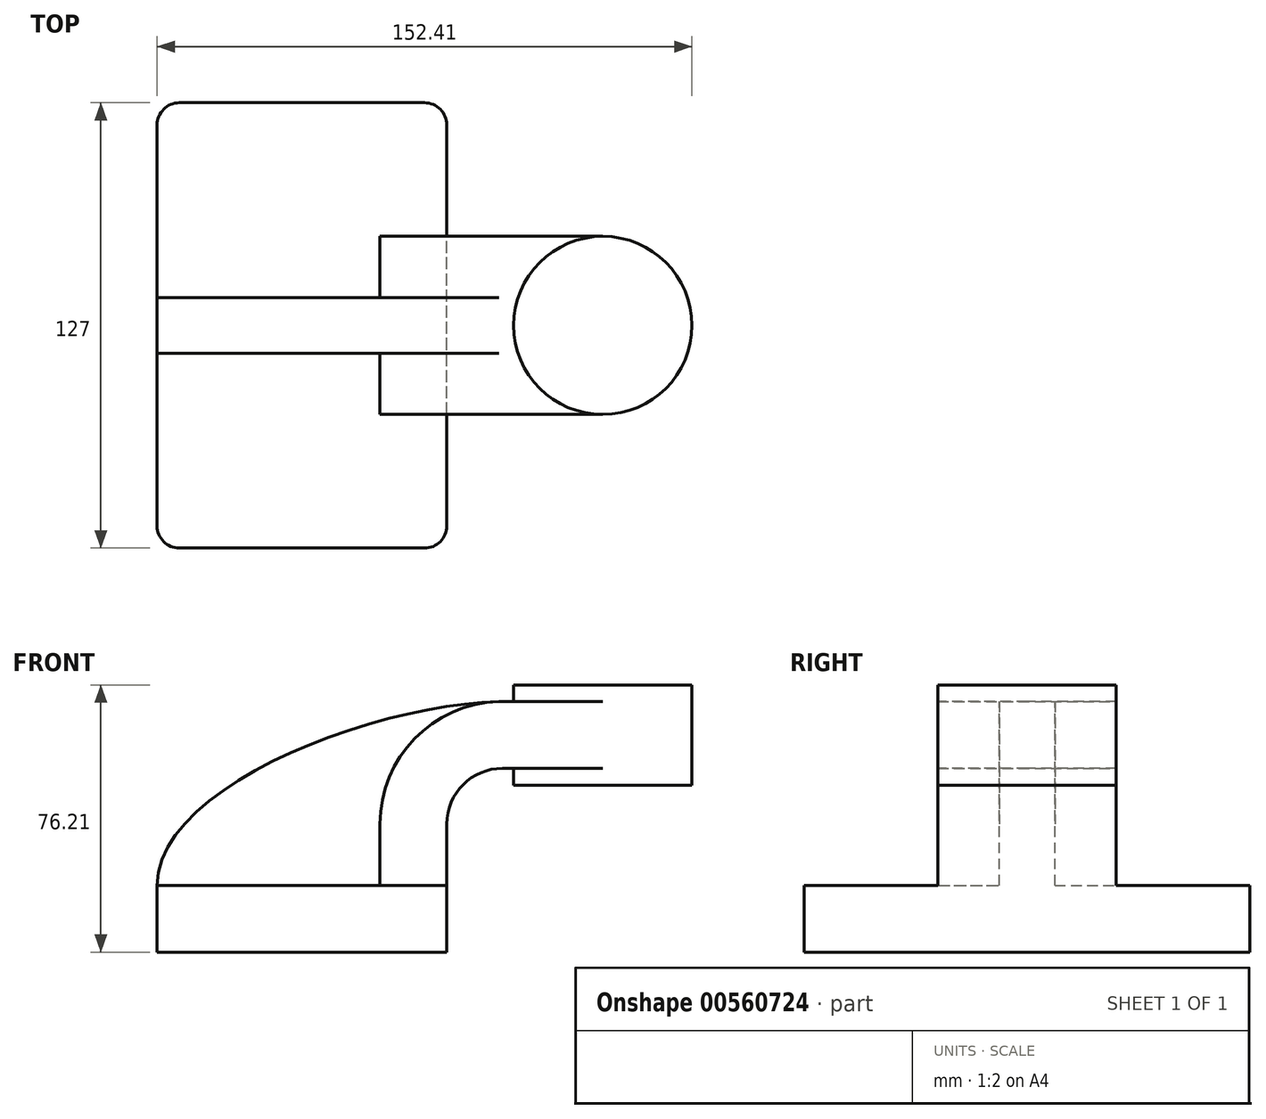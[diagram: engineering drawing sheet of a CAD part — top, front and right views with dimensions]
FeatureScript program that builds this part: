
annotation { "Feature Type Name" : "Feature", "Feature Type Description" : "" }
export const myFeature = defineFeature(function(context is Context, id is Id, definition is map)
    precondition{}
    {
        {
            var Q0;
            Q0=qCreatedBy(makeId("Front.planeOp"),FACE);
            var sketch = newSketch(context, id + "F0", { "sketchPlane" : qUnion([Q0])});
            skLineSegment(sketch, "E0.bottom", {"start": v(41.28, -9.52) * mm, "end": v(-41.28, -9.53) * mm});
            skLineSegment(sketch, "E0.top", {"start": v(41.27, 9.53) * mm, "end": v(-41.28, 9.53) * mm});
            skLineSegment(sketch, "E0.left", {"start": v(41.28, -9.52) * mm, "end": v(41.28, 9.53) * mm});
            skLineSegment(sketch, "E0.right", {"start": v(-41.28, -9.52) * mm, "end": v(-41.28, 9.53) * mm});
            skPoint(sketch, "E0.middle", {"position": v(0, 0) * mm});
            skLineSegment(sketch, "E1.bottom", {"start": v(60.32, 38.1) * mm, "end": v(111.12, 38.1) * mm});
            skLineSegment(sketch, "E1.top", {"start": v(60.32, 66.68) * mm, "end": v(111.12, 66.68) * mm});
            skLineSegment(sketch, "E1.left", {"start": v(60.32, 38.1) * mm, "end": v(60.32, 66.68) * mm});
            skLineSegment(sketch, "E1.right", {"start": v(111.12, 38.1) * mm, "end": v(111.12, 66.68) * mm});
            skPoint(sketch, "E1.middle", {"position": v(85.72, 52.39) * mm});
            skLineSegment(sketch, "E2", {"start": v(41.27, 9.53) * mm, "end": v(41.27, 27) * mm});
            skArc(sketch, "E3", {"start": v(41.27, 27) * mm, "mid": v(45.92, 38.23) * mm, "end": v(57.15, 42.88) * mm});
            skLineSegment(sketch, "E4", {"start": v(57.15, 42.88) * mm, "end": v(85.72, 42.88) * mm});
            skLineSegment(sketch, "E5.0", {"start": v(57.15, 61.93) * mm, "end": v(85.72, 61.93) * mm});
            skArc(sketch, "E5.1", {"start": v(22.23, 27) * mm, "mid": v(32.45, 51.7) * mm, "end": v(57.15, 61.93) * mm});
            skLineSegment(sketch, "E5.2", {"start": v(22.23, 9.53) * mm, "end": v(22.23, 27) * mm});
            skFitSpline(sketch, "E6", {"points": [v(-41.28, 9.53) * mm, v(57.15, 61.93) * mm], "startDerivative": vector(0.33, 86.27) * mm, "endDerivative": vector(105.39, 0.93) * mm});
            skLineSegment(sketch, "E7", {"start": v(85.72, 38.1) * mm, "end": v(85.72, 66.68) * mm});
            skSolve(sketch);
        }
        {
            var Q0;
            Q0=makeQuery(id+"F0.imprint","IMPRINT",FACE,{"disambiguationData":[TD([[makeQuery(id+"F0.imprint","IMPRINT",EDGE,{"derivedFrom":sQuery(id+"F0.wireOp",EDGE,"E0.bottom")}),-1.0]])]});
            extrude(context, id + "F1", {"entities" : qUnion([Q0]), "endBound" : BoundingType.SYMMETRIC, "depth" : 127 * mm, "offsetDistance" : 25.4 * mm});
        }
        {
            var Q0;
            {var subQ0=sQuery(id+"F0.wireOp",EDGE,"E4");var subQ1=sQuery(id+"F0.wireOp",EDGE,"E1.left");var subQ2=makeQuery(id+"F0.imprint","INTERSECT",VERTEX,{"derivedFrom":[subQ1,subQ0]});Q0=makeQuery(id+"F0.imprint","IMPRINT",FACE,{"disambiguationData":[TD([[makeQuery(id+"F0.imprint","IMPRINT",EDGE,{"disambiguationData":[TD([[subQ2,-1.0]])],"derivedFrom":subQ1}),-1.0]])]});}
            var Q1;
            {var subQ1=sQuery(id+"F0.wireOp",EDGE,"E2");Q1=makeQuery(id+"F0.imprint","IMPRINT",FACE,{"disambiguationData":[TD([[makeQuery(id+"F0.imprint","IMPRINT",EDGE,{"derivedFrom":subQ1}),1.0]])]});}
            extrude(context, id + "F2", {"entities" : qUnion([Q0, Q1]), "operationType" : NewBodyOperationType.ADD, "endBound" : BoundingType.SYMMETRIC, "depth" : 50.8 * mm, "offsetDistance" : 25.4 * mm});
        }
        {
            var Q0;
            {var subQ3=sQuery(id+"F0.wireOp",EDGE,"E5.2");Q0=makeQuery(id+"F0.imprint","IMPRINT",FACE,{"disambiguationData":[TD([[makeQuery(id+"F0.imprint","IMPRINT",EDGE,{"derivedFrom":subQ3}),1.0]])]});}
            extrude(context, id + "F3", {"entities" : qUnion([Q0]), "operationType" : NewBodyOperationType.ADD, "endBound" : BoundingType.SYMMETRIC, "depth" : 15.88 * mm, "offsetDistance" : 25.4 * mm});
        }
        {
            var Q0;
            {var subQ4=sQuery(id+"F0.wireOp",EDGE,"E1.right");Q0=makeQuery(id+"F0.imprint","IMPRINT",FACE,{"disambiguationData":[TD([[makeQuery(id+"F0.imprint","IMPRINT",EDGE,{"derivedFrom":subQ4}),1.0]])]});}
            var Q1;
            Q1=sQuery(id+"F0.wireOp",EDGE,"E7");
            revolve(context, id + "F4", {"operationType" : NewBodyOperationType.ADD, "entities" : qUnion([Q0]), "axis" : qUnion([Q1]), "revolveType" : RevolveType.FULL});
        }
        {
            var Q0;
            Q0=makeQuery(id+"F1.opExtrude","CAP_EDGE",EDGE,{"disambiguationData":[OSD([sQuery(id+"F0.wireOp",EDGE,"E0.right")])],"isStart":false});
            var Q1;
            Q1=makeQuery(id+"F1.opExtrude","CAP_EDGE",EDGE,{"disambiguationData":[OSD([sQuery(id+"F0.wireOp",EDGE,"E0.left")])],"isStart":false});
            var Q2;
            Q2=makeQuery(id+"F1.opExtrude","CAP_EDGE",EDGE,{"disambiguationData":[OSD([sQuery(id+"F0.wireOp",EDGE,"E0.left")])],"isStart":true});
            var Q3;
            Q3=makeQuery(id+"F1.opExtrude","CAP_EDGE",EDGE,{"disambiguationData":[OSD([sQuery(id+"F0.wireOp",EDGE,"E0.right")])],"isStart":true});
            fillet(context, id + "F5", {"entities" : qUnion([Q0, Q1, Q2, Q3]), "radius" : 6.35 * mm, "tangentPropagation" : true, "allowEdgeOverflow" : false});
        }
    });
